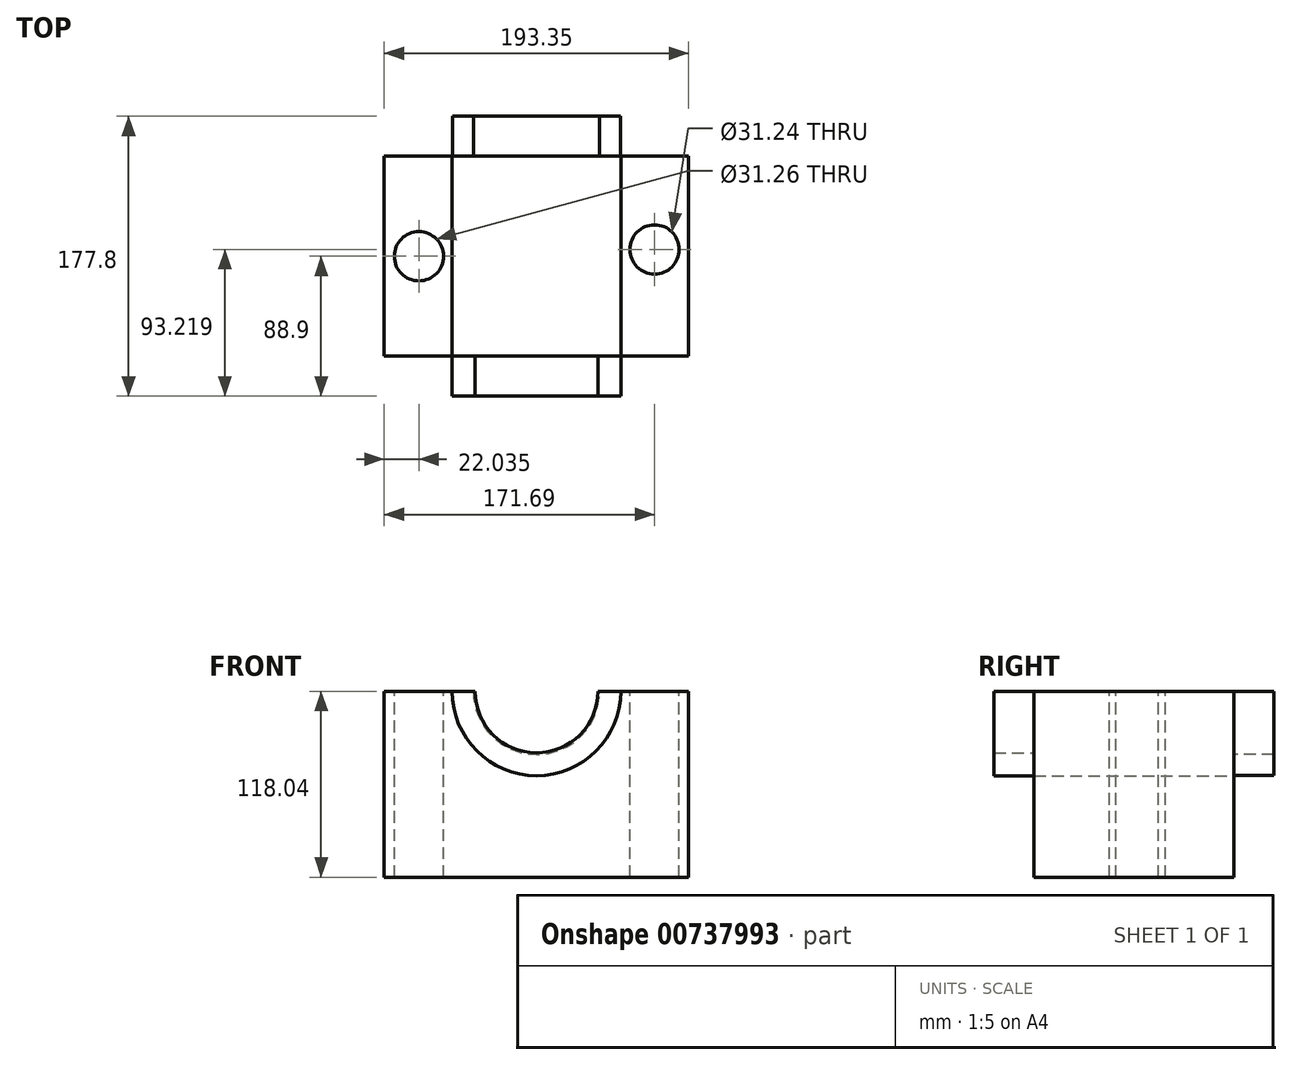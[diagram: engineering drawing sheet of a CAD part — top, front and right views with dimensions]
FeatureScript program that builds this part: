
annotation { "Feature Type Name" : "Feature", "Feature Type Description" : "" }
export const myFeature = defineFeature(function(context is Context, id is Id, definition is map)
    precondition{}
    {
        {
            var Q0;
            Q0=qCreatedBy(makeId("Front.planeOp"),FACE);
            var sketch = newSketch(context, id + "F0", { "sketchPlane" : qUnion([Q0])});
            skLineSegment(sketch, "E0.bottom", {"start": v(-91.7, 30.08) * mm, "end": v(101.65, 30.08) * mm});
            skLineSegment(sketch, "E0.top", {"start": v(-91.7, -87.96) * mm, "end": v(101.65, -87.96) * mm});
            skLineSegment(sketch, "E0.left", {"start": v(-91.7, 30.08) * mm, "end": v(-91.7, -87.96) * mm});
            skLineSegment(sketch, "E0.right", {"start": v(101.65, 30.08) * mm, "end": v(101.65, -87.96) * mm});
            skSolve(sketch);
        }
        {
            var Q0;
            Q0=makeQuery(id+"F0.imprint","IMPRINT",FACE,{"disambiguationData":[TD([[makeQuery(id+"F0.imprint","IMPRINT",EDGE,{"derivedFrom":sQuery(id+"F0.wireOp",EDGE,"E0.bottom")}),-1.0]])]});
            extrude(context, id + "F1", {"entities" : qUnion([Q0]), "oppositeDirection" : true, "depth" : 127 * mm, "offsetDistance" : 25.4 * mm});
        }
        {
            var Q0;
            Q0=makeQuery(id+"F1.opExtrude","CAP_FACE",FACE,{"disambiguationData":[OSD([sQuery(id+"F0.wireOp",EDGE,"E0.bottom"),sQuery(id+"F0.wireOp",EDGE,"E0.top"),sQuery(id+"F0.wireOp",EDGE,"E0.left"),sQuery(id+"F0.wireOp",EDGE,"E0.right")])],"isStart":false});
            var sketch = newSketch(context, id + "F2", { "sketchPlane" : qUnion([Q0])});
            skArc(sketch, "E1", {"start": v(-58.53, 30.08) * mm, "mid": v(-4.98, -23.47) * mm, "end": v(48.57, 30.08) * mm});
            skLineSegment(sketch, "E2", {"start": v(-58.53, 30.08) * mm, "end": v(48.57, 30.08) * mm});
            skSolve(sketch);
        }
        {
            var Q0;
            Q0=makeQuery(id+"F2.imprint","IMPRINT",FACE,{"disambiguationData":[TD([[makeQuery(id+"F2.imprint","IMPRINT",EDGE,{"derivedFrom":sQuery(id+"F2.wireOp",EDGE,"E1")}),1.0]])]});
            extrude(context, id + "F3", {"entities" : qUnion([Q0]), "operationType" : NewBodyOperationType.REMOVE, "oppositeDirection" : true, "depth" : 127 * mm, "offsetDistance" : 25.4 * mm});
        }
        {
            var Q0;
            Q0=makeQuery(id+"F1.opExtrude","CAP_FACE",FACE,{"disambiguationData":[OSD([sQuery(id+"F0.wireOp",EDGE,"E0.bottom"),sQuery(id+"F0.wireOp",EDGE,"E0.top"),sQuery(id+"F0.wireOp",EDGE,"E0.left"),sQuery(id+"F0.wireOp",EDGE,"E0.right")])],"isStart":false});
            var sketch = newSketch(context, id + "F4", { "sketchPlane" : qUnion([Q0])});
            skArc(sketch, "E3", {"start": v(-58.33, 30.08) * mm, "mid": v(-4.98, -23.27) * mm, "end": v(48.37, 30.08) * mm});
            skLineSegment(sketch, "E4", {"start": v(-58.53, 30.08) * mm, "end": v(-45.05, 30.08) * mm});
            skLineSegment(sketch, "E5", {"start": v(48.57, 30.08) * mm, "end": v(35.1, 30.08) * mm});
            skArc(sketch, "E6", {"start": v(-45.05, 30.08) * mm, "mid": v(-4.98, -10) * mm, "end": v(35.1, 30.08) * mm});
            skLineSegment(sketch, "E7.trimOffspring", {"start": v(35.1, 30.08) * mm, "end": v(48.57, 30.08) * mm});
            skSolve(sketch);
        }
        {
            var Q0;
            {var subQ0=sQuery(id+"F4.wireOp",EDGE,"E3");Q0=makeQuery(id+"F4.imprint","IMPRINT",FACE,{"disambiguationData":[TD([[makeQuery(id+"F4.imprint","IMPRINT",EDGE,{"derivedFrom":subQ0}),1.0]])]});}
            extrude(context, id + "F5", {"entities" : qUnion([Q0]), "depth" : 25.4 * mm, "offsetDistance" : 25.4 * mm});
        }
        {
            var Q0;
            Q0=makeQuery(id+"F1.opExtrude","CAP_FACE",FACE,{"disambiguationData":[OSD([sQuery(id+"F0.wireOp",EDGE,"E0.bottom"),sQuery(id+"F0.wireOp",EDGE,"E0.top"),sQuery(id+"F0.wireOp",EDGE,"E0.left"),sQuery(id+"F0.wireOp",EDGE,"E0.right")])],"isStart":true});
            var sketch = newSketch(context, id + "F6", { "sketchPlane" : qUnion([Q0])});
            skArc(sketch, "E8", {"start": v(-33.98, 30.08) * mm, "mid": v(4.98, -8.88) * mm, "end": v(43.94, 30.08) * mm});
            skLineSegment(sketch, "E9", {"start": v(4.98, 30.08) * mm, "end": v(-33.98, 30.08) * mm});
            skLineSegment(sketch, "E10", {"start": v(-33.98, 30.08) * mm, "end": v(43.94, 30.08) * mm});
            skArc(sketch, "E11", {"start": v(-48.57, 30.08) * mm, "mid": v(4.98, -23.47) * mm, "end": v(58.53, 30.08) * mm});
            skLineSegment(sketch, "E12", {"start": v(-48.57, 30.08) * mm, "end": v(58.53, 30.08) * mm});
            skSolve(sketch);
        }
        {
            var Q0;
            {var subQ0=sQuery(id+"F6.wireOp",EDGE,"E8");Q0=makeQuery(id+"F6.imprint","IMPRINT",FACE,{"disambiguationData":[TD([[makeQuery(id+"F6.imprint","IMPRINT",EDGE,{"derivedFrom":subQ0}),-1.0]])]});}
            extrude(context, id + "F7", {"entities" : qUnion([Q0]), "depth" : 25.4 * mm, "offsetDistance" : 25.4 * mm});
        }
        {
            var Q0;
            {var subQ1=sQuery(id+"F0.wireOp",EDGE,"E0.left");var subQ3=sQuery(id+"F0.wireOp",EDGE,"E0.bottom");Q0=makeQuery(id+"F3.boolean.opBoolean","SPLIT",FACE,{"disambiguationData":[TD([makeQuery(id+"F1.opExtrude","SWEPT_FACE",FACE,{"disambiguationData":[OSD([subQ1])]})])],"derivedFrom":makeQuery(id+"F1.opExtrude","SWEPT_FACE",FACE,{"disambiguationData":[OSD([subQ3])]})});}
            var sketch = newSketch(context, id + "F8", { "sketchPlane" : qUnion([Q0])});
            skCircle(sketch, "E13", {"center": v(-69.67, 63.5) * mm, "radius": 15.63 * mm});
            skPoint(sketch, "E13.centerSnap0", {"position": v(-48.57, 63.5) * mm});
            skCircle(sketch, "E14", {"center": v(80, 67.82) * mm, "radius": 15.62 * mm});
            skSolve(sketch);
        }
        {
            var Q0;
            Q0=makeQuery(id+"F8.imprint","IMPRINT",FACE,{"disambiguationData":[TD([[makeQuery(id+"F8.imprint","IMPRINT",EDGE,{"derivedFrom":sQuery(id+"F8.wireOp",EDGE,"E13")}),1.0]])]});
            var Q1;
            Q1=makeQuery(id+"F8.imprint","IMPRINT",FACE,{"disambiguationData":[TD([[makeQuery(id+"F8.imprint","IMPRINT",EDGE,{"derivedFrom":sQuery(id+"F8.wireOp",EDGE,"E14")}),1.0]])]});
            var Q2;
            Q2 = qSketchRegion(id + "F8", true);
            extrude(context, id + "F9", {"entities" : qUnion([Q0, Q1, Q2]), "operationType" : NewBodyOperationType.REMOVE, "oppositeDirection" : true, "depth" : 254 * mm, "offsetDistance" : 25.4 * mm});
        }
    });
